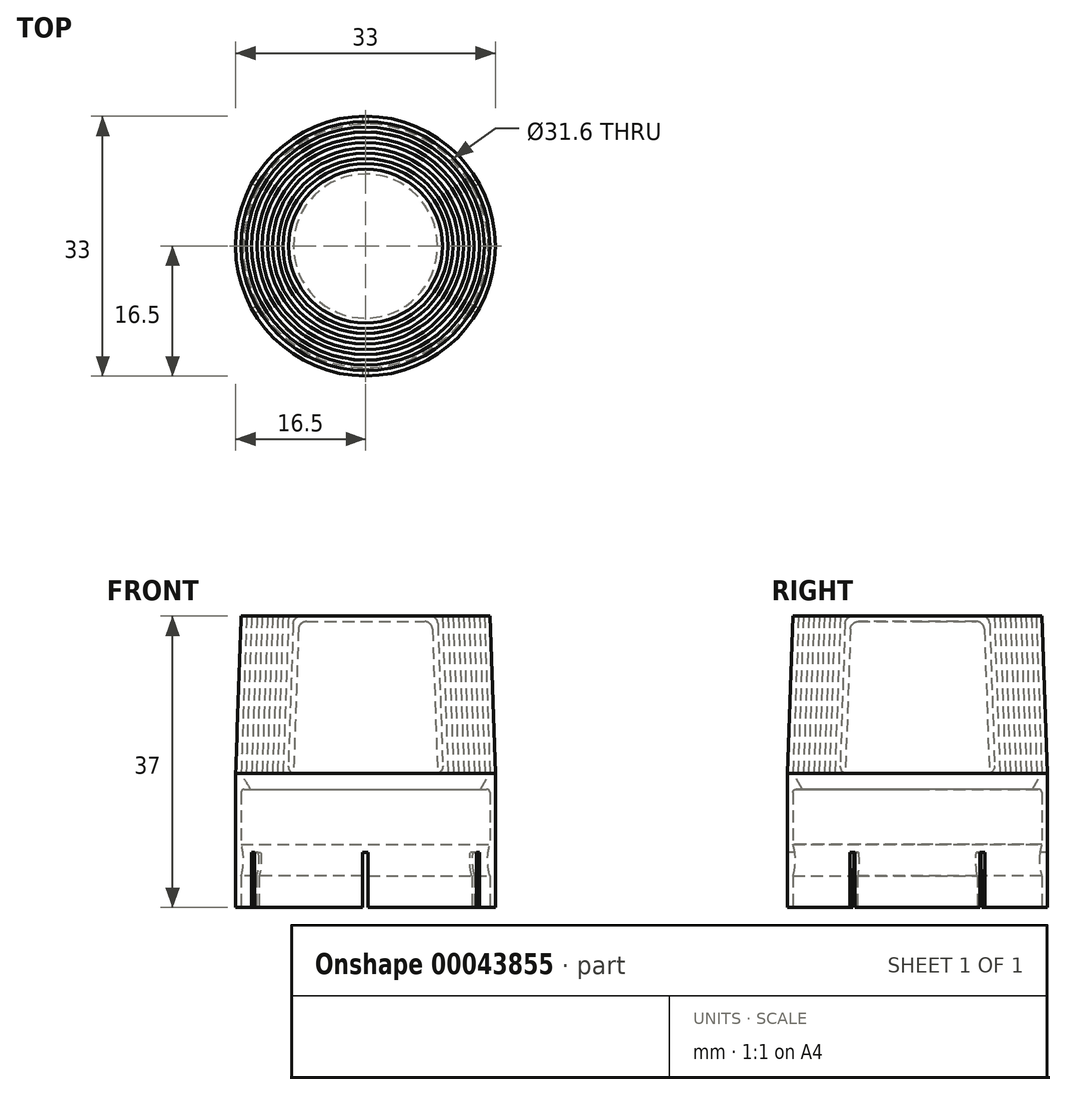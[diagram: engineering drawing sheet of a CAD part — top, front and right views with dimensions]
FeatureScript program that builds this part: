
annotation { "Feature Type Name" : "Feature", "Feature Type Description" : "" }
export const myFeature = defineFeature(function(context is Context, id is Id, definition is map)
    precondition{}
    {
        {
            var Q0;
            Q0=qCreatedBy(makeId("Front.planeOp"),FACE);
            var sketch = newSketch(context, id + "F0", { "sketchPlane" : qUnion([Q0])});
            skLineSegment(sketch, "E0", {"start": v(0, 0) * mm, "end": v(0, 9.2) * mm, "construction": true});
            skLineSegment(sketch, "E1.rect.bottom", {"start": v(-9.85, 10) * mm, "end": v(9.85, 10) * mm, "construction": true});
            skLineSegment(sketch, "E1.rect.top", {"start": v(-9.85, -10) * mm, "end": v(9.85, -10) * mm, "construction": true});
            skLineSegment(sketch, "E1.rect.left", {"start": v(-9.85, 10) * mm, "end": v(-9.85, -10) * mm, "construction": true});
            skLineSegment(sketch, "E1.rect.right", {"start": v(9.85, 10) * mm, "end": v(9.85, -10) * mm, "construction": true});
            skPoint(sketch, "E1.rect.middle", {"position": v(0, 0) * mm});
            skLineSegment(sketch, "E2", {"start": v(-9.85, -10) * mm, "end": v(-9.15, 10) * mm});
            skLineSegment(sketch, "E3", {"start": v(-9.15, 10) * mm, "end": v(-8.45, 10) * mm});
            skLineSegment(sketch, "E4", {"start": v(-8.45, 10) * mm, "end": v(-9.15, -10) * mm});
            skLineSegment(sketch, "E5", {"start": v(-9.15, -10) * mm, "end": v(-9.85, -10) * mm});
            skLineSegment(sketch, "E6", {"start": v(-9.15, 10) * mm, "end": v(-9.85, 10) * mm});
            skLineSegment(sketch, "E7.1.0.0", {"start": v(-10.48, 10) * mm, "end": v(-9.78, 10) * mm});
            skLineSegment(sketch, "E7.1.0.1", {"start": v(-11.18, -10) * mm, "end": v(-10.48, 10) * mm});
            skLineSegment(sketch, "E7.1.0.2", {"start": v(-9.78, 10) * mm, "end": v(-10.48, -10) * mm});
            skLineSegment(sketch, "E7.1.0.3", {"start": v(-10.48, -10) * mm, "end": v(-11.18, -10) * mm});
            skLineSegment(sketch, "E7.2.0.0", {"start": v(-11.8, 10) * mm, "end": v(-11.1, 10) * mm});
            skLineSegment(sketch, "E7.2.0.1", {"start": v(-12.5, -10) * mm, "end": v(-11.8, 10) * mm});
            skLineSegment(sketch, "E7.2.0.2", {"start": v(-11.1, 10) * mm, "end": v(-11.8, -10) * mm});
            skLineSegment(sketch, "E7.2.0.3", {"start": v(-11.8, -10) * mm, "end": v(-12.5, -10) * mm});
            skLineSegment(sketch, "E7.3.0.0", {"start": v(-13.14, 10) * mm, "end": v(-12.44, 10) * mm});
            skLineSegment(sketch, "E7.3.0.1", {"start": v(-13.84, -10) * mm, "end": v(-13.14, 10) * mm});
            skLineSegment(sketch, "E7.3.0.2", {"start": v(-12.44, 10) * mm, "end": v(-13.14, -10) * mm});
            skLineSegment(sketch, "E7.3.0.3", {"start": v(-13.14, -10) * mm, "end": v(-13.84, -10) * mm});
            skLineSegment(sketch, "E7.4.0.0", {"start": v(-14.47, 10) * mm, "end": v(-13.77, 10) * mm});
            skLineSegment(sketch, "E7.4.0.1", {"start": v(-15.17, -10) * mm, "end": v(-14.47, 10) * mm});
            skLineSegment(sketch, "E7.4.0.2", {"start": v(-13.77, 10) * mm, "end": v(-14.47, -10) * mm});
            skLineSegment(sketch, "E7.4.0.3", {"start": v(-14.47, -10) * mm, "end": v(-15.17, -10) * mm});
            skLineSegment(sketch, "E7.5.0.0", {"start": v(-15.8, 10) * mm, "end": v(-15.1, 10) * mm});
            skLineSegment(sketch, "E7.5.0.1", {"start": v(-16.5, -10) * mm, "end": v(-15.8, 10) * mm});
            skLineSegment(sketch, "E7.5.0.2", {"start": v(-15.1, 10) * mm, "end": v(-15.8, -10) * mm});
            skLineSegment(sketch, "E7.5.0.3", {"start": v(-15.8, -10) * mm, "end": v(-16.5, -10) * mm});
            skLineSegment(sketch, "E7.direction1", {"start": v(-9.15, 10) * mm, "end": v(-10.48, 10) * mm, "construction": true});
            skLineSegment(sketch, "E8", {"start": v(-9.15, 10) * mm, "end": v(0, 10) * mm});
            skLineSegment(sketch, "E9", {"start": v(0, 10) * mm, "end": v(0, 9.3) * mm});
            skLineSegment(sketch, "E10", {"start": v(0, 9.3) * mm, "end": v(-9.17, 9.3) * mm});
            skLineSegment(sketch, "E11.top", {"start": v(-15.8, -27) * mm, "end": v(-16.5, -27) * mm});
            skLineSegment(sketch, "E11.left", {"start": v(-15.8, -12.4) * mm, "end": v(-15.8, -27) * mm});
            skLineSegment(sketch, "E11.right", {"start": v(-16.5, -10) * mm, "end": v(-16.5, -27) * mm});
            skArc(sketch, "E12", {"start": v(-15.8, -23) * mm, "mid": v(-15.5, -21) * mm, "end": v(-15.8, -19) * mm});
            skLineSegment(sketch, "E13", {"start": v(-15.8, -10) * mm, "end": v(-14.6, -12) * mm});
            skLineSegment(sketch, "E14", {"start": v(-14.6, -12) * mm, "end": v(-15.4, -12) * mm});
            skLineSegment(sketch, "E15", {"start": v(-15.8, -12) * mm, "end": v(-15.8, -10) * mm});
            skPoint(sketch, "E16.newPointA", {"position": v(-15.8, -12) * mm});
            skArc(sketch, "E16.filletArc", {"start": v(-15.4, -12) * mm, "mid": v(-15.68, -12.12) * mm, "end": v(-15.8, -12.4) * mm});
            skSolve(sketch);
        }
        {
            var Q0;
            Q0=makeQuery(id+"F0.imprint","IMPRINT",FACE,{"disambiguationData":[TD([[makeQuery(id+"F0.imprint","IMPRINT",EDGE,{"derivedFrom":sQuery(id+"F0.wireOp",EDGE,"E7.5.0.0")}),-1.0]])]});
            var Q1;
            Q1=makeQuery(id+"F0.imprint","IMPRINT",FACE,{"disambiguationData":[TD([[makeQuery(id+"F0.imprint","IMPRINT",EDGE,{"derivedFrom":sQuery(id+"F0.wireOp",EDGE,"E7.4.0.0")}),-1.0]])]});
            var Q2;
            Q2=makeQuery(id+"F0.imprint","IMPRINT",FACE,{"disambiguationData":[TD([[makeQuery(id+"F0.imprint","IMPRINT",EDGE,{"derivedFrom":sQuery(id+"F0.wireOp",EDGE,"E7.3.0.0")}),-1.0]])]});
            var Q3;
            Q3=makeQuery(id+"F0.imprint","IMPRINT",FACE,{"disambiguationData":[TD([[makeQuery(id+"F0.imprint","IMPRINT",EDGE,{"derivedFrom":sQuery(id+"F0.wireOp",EDGE,"E7.2.0.0")}),-1.0]])]});
            var Q4;
            {var subQ2=sQuery(id+"F0.wireOp",EDGE,"E7.1.0.1");Q4=makeQuery(id+"F0.imprint","IMPRINT",FACE,{"disambiguationData":[TD([[makeQuery(id+"F0.imprint","IMPRINT",EDGE,{"derivedFrom":subQ2}),-1.0]])]});}
            var Q5;
            {var subQ5=sQuery(id+"F0.wireOp",EDGE,"E5");Q5=makeQuery(id+"F0.imprint","IMPRINT",FACE,{"disambiguationData":[TD([[makeQuery(id+"F0.imprint","IMPRINT",EDGE,{"derivedFrom":subQ5}),-1.0]])]});}
            var Q6;
            {var subQ3=sQuery(id+"F0.wireOp",EDGE,"E2");var subQ5=sQuery(id+"F0.wireOp",EDGE,"E8");var subQ7=makeQuery(id+"F0.imprint","INTERSECT",VERTEX,{"derivedFrom":[subQ3,subQ5]});Q6=makeQuery(id+"F0.imprint","IMPRINT",FACE,{"disambiguationData":[TD([[makeQuery(id+"F0.imprint","IMPRINT",EDGE,{"disambiguationData":[TD([[subQ7,1.0]])],"derivedFrom":subQ3}),-1.0]])]});}
            var Q7;
            {var subQ3=sQuery(id+"F0.wireOp",EDGE,"E9");Q7=makeQuery(id+"F0.imprint","IMPRINT",FACE,{"disambiguationData":[TD([[makeQuery(id+"F0.imprint","IMPRINT",EDGE,{"derivedFrom":subQ3}),-1.0]])]});}
            var Q8;
            {var subQ0=sQuery(id+"F0.wireOp",EDGE,"E12");Q8=makeQuery(id+"F0.imprint","IMPRINT",FACE,{"disambiguationData":[TD([[makeQuery(id+"F0.imprint","IMPRINT",EDGE,{"derivedFrom":subQ0}),1.0]])]});}
            var Q9;
            {var subQ0=sQuery(id+"F0.wireOp",EDGE,"ff47ce86-b8d3-4464-82e5-28207d753c21");Q9=makeQuery(id+"F0.imprint","IMPRINT",FACE,{"disambiguationData":[TD([[makeQuery(id+"F0.imprint","IMPRINT",EDGE,{"derivedFrom":subQ0}),1.0]])]});}
            var Q10;
            Q10=makeQuery(id+"F0.imprint","IMPRINT",FACE,{"disambiguationData":[TD([[makeQuery(id+"F0.imprint","IMPRINT",EDGE,{"derivedFrom":sQuery(id+"F0.wireOp",EDGE,"E7.5.0.3")}),1.0]])]});
            var Q11;
            Q11=sQuery(id+"F0.wireOp",EDGE,"E0");
            revolve(context, id + "F1", {"entities" : qUnion([Q0, Q1, Q2, Q3, Q4, Q5, Q6, Q7, Q8, Q9, Q10]), "axis" : qUnion([Q11]), "revolveType" : RevolveType.FULL});
        }
        {
            var Q0;
            Q0=makeQuery(id+"F1.opRevolve","SWEPT_EDGE",EDGE,{"disambiguationData":[OSD([sQuery(id+"F0.wireOp",EDGE,"E2"),sQuery(id+"F0.wireOp",EDGE,"E8")])]});
            var Q1;
            Q1=makeQuery(id+"F1.opRevolve","SWEPT_EDGE",EDGE,{"disambiguationData":[OSD([sQuery(id+"F0.wireOp",EDGE,"E4"),sQuery(id+"F0.wireOp",EDGE,"E10")])]});
            fillet(context, id + "F2", {"entities" : qUnion([Q0, Q1]), "radius" : 1 * mm, "tangentPropagation" : true, "allowEdgeOverflow" : false});
        }
        {
            var Q0;
            Q0=makeQuery(id+"F1.opRevolve","SWEPT_FACE",FACE,{"disambiguationData":[OSD([sQuery(id+"F0.wireOp",EDGE,"E11.top")])]});
            var sketch = newSketch(context, id + "F3", { "sketchPlane" : qUnion([Q0])});
            skLineSegment(sketch, "E17.rect.bottom", {"start": v(0.35, -20) * mm, "end": v(-0.35, -20) * mm});
            skLineSegment(sketch, "E17.rect.top", {"start": v(0.35, 20) * mm, "end": v(-0.35, 20) * mm});
            skLineSegment(sketch, "E17.rect.left", {"start": v(0.35, -20) * mm, "end": v(0.35, 20) * mm});
            skLineSegment(sketch, "E17.rect.right", {"start": v(-0.35, -20) * mm, "end": v(-0.35, 20) * mm});
            skPoint(sketch, "E17.rect.middle", {"position": v(0, 0) * mm});
            skLineSegment(sketch, "E18.1.0", {"start": v(17.5, 9.7) * mm, "end": v(-17.15, -10.3) * mm});
            skLineSegment(sketch, "E18.1.1", {"start": v(17.15, 10.3) * mm, "end": v(-17.5, -9.7) * mm});
            skLineSegment(sketch, "E18.1.2", {"start": v(-17.5, -9.7) * mm, "end": v(-17.15, -10.3) * mm});
            skLineSegment(sketch, "E18.1.3", {"start": v(17.15, 10.3) * mm, "end": v(17.5, 9.7) * mm});
            skLineSegment(sketch, "E18.2.0", {"start": v(-17.15, 10.3) * mm, "end": v(17.5, -9.7) * mm});
            skLineSegment(sketch, "E18.2.1", {"start": v(-17.5, 9.7) * mm, "end": v(17.15, -10.3) * mm});
            skLineSegment(sketch, "E18.2.2", {"start": v(17.15, -10.3) * mm, "end": v(17.5, -9.7) * mm});
            skLineSegment(sketch, "E18.2.3", {"start": v(-17.5, 9.7) * mm, "end": v(-17.15, 10.3) * mm});
            skSolve(sketch);
        }
        {
            var Q0;
            Q0 = qSketchRegion(id + "F3", true);
            extrude(context, id + "F4", {"entities" : qUnion([Q0]), "operationType" : NewBodyOperationType.REMOVE, "oppositeDirection" : true, "depth" : 7 * mm});
        }
    });
